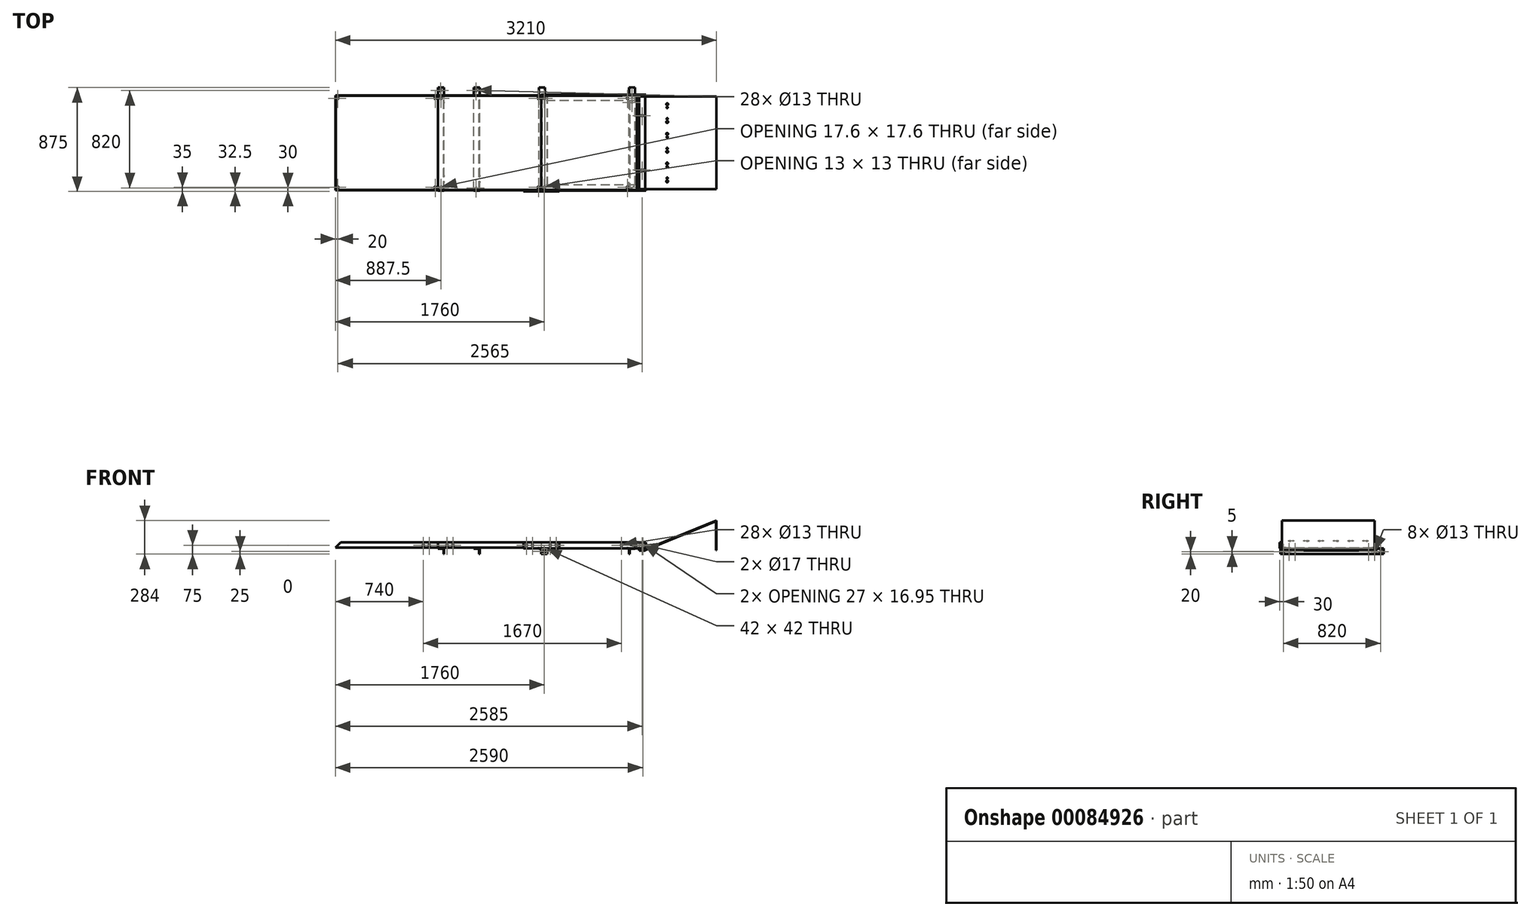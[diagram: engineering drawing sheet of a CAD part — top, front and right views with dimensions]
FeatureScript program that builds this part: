
annotation { "Feature Type Name" : "Feature", "Feature Type Description" : "" }
export const myFeature = defineFeature(function(context is Context, id is Id, definition is map)
    precondition{}
    {
        {
            var Q0;
            Q0=qCreatedBy(makeId("Front.planeOp"),FACE);
            var sketch = newSketch(context, id + "F0", { "sketchPlane" : qUnion([Q0])});
            skLineSegment(sketch, "E0", {"start": v(0, 0) * mm, "end": v(0, 4) * mm});
            skLineSegment(sketch, "E1", {"start": v(0, 4) * mm, "end": v(50, 4) * mm});
            skLineSegment(sketch, "E2", {"start": v(50, 4) * mm, "end": v(650, 250) * mm});
            skLineSegment(sketch, "E3", {"start": v(650, 250) * mm, "end": v(650, 0) * mm});
            skLineSegment(sketch, "E4", {"start": v(650, 0) * mm, "end": v(646, 0) * mm});
            skLineSegment(sketch, "E5", {"start": v(646, 0) * mm, "end": v(646, 244.04) * mm});
            skLineSegment(sketch, "E6", {"start": v(646, 244.04) * mm, "end": v(50.79, 0) * mm});
            skLineSegment(sketch, "E7", {"start": v(50.79, 0) * mm, "end": v(0, 0) * mm});
            skSolve(sketch);
        }
        {
            var Q0;
            Q0 = qSketchRegion(id + "F0", true);
            extrude(context, id + "F1", {"entities" : qUnion([Q0]), "oppositeDirection" : true, "depth" : 780 * mm});
        }
        {
            var Q0;
            Q0=qCreatedBy(makeId("Right.planeOp"),FACE);
            var sketch = newSketch(context, id + "F2", { "sketchPlane" : qUnion([Q0])});
            skLineSegment(sketch, "E8", {"start": v(0, 0) * mm, "end": v(-7, 0) * mm});
            skLineSegment(sketch, "E9", {"start": v(-7, 0) * mm, "end": v(-7, 66) * mm});
            skLineSegment(sketch, "E10", {"start": v(-7, 66) * mm, "end": v(-11, 66) * mm});
            skLineSegment(sketch, "E11", {"start": v(-11, 66) * mm, "end": v(-11, -4) * mm});
            skLineSegment(sketch, "E12", {"start": v(-11, -4) * mm, "end": v(791, -4) * mm});
            skLineSegment(sketch, "E13", {"start": v(791, -4) * mm, "end": v(791, 66) * mm});
            skLineSegment(sketch, "E14", {"start": v(791, 66) * mm, "end": v(787, 66) * mm});
            skLineSegment(sketch, "E15", {"start": v(787, 66) * mm, "end": v(787, 0) * mm});
            skLineSegment(sketch, "E16", {"start": v(787, 0) * mm, "end": v(0, 0) * mm});
            skSolve(sketch);
        }
        {
            var Q0;
            Q0=makeQuery(id+"F2.imprint","IMPRINT",FACE,{"disambiguationData":[TD([[makeQuery(id+"F2.imprint","IMPRINT",EDGE,{"derivedFrom":sQuery(id+"F2.wireOp",EDGE,"E8")}),1.0]])]});
            extrude(context, id + "F3", {"entities" : qUnion([Q0]), "depth" : 50 * mm});
        }
        {
            var Q0;
            Q0=makeQuery(id+"F3.opExtrude","SWEPT_FACE",FACE,{"disambiguationData":[OSD([sQuery(id+"F2.wireOp",EDGE,"E11")])]});
            var sketch = newSketch(context, id + "F4", { "sketchPlane" : qUnion([Q0])});
            skCircle(sketch, "E17", {"center": v(20, 41) * mm, "radius": 8.5 * mm});
            skSolve(sketch);
        }
        {
            var Q0;
            Q0 = qSketchRegion(id + "F4", true);
            extrude(context, id + "F5", {"entities" : qUnion([Q0]), "operationType" : NewBodyOperationType.REMOVE, "endBound" : BoundingType.THROUGH_ALL, "oppositeDirection" : true, "depth" : 25 * mm});
        }
        {
            var Q0;
            Q0=makeQuery(id+"F3.opExtrude","SWEPT_FACE",FACE,{"disambiguationData":[OSD([sQuery(id+"F2.wireOp",EDGE,"E11")])]});
            var sketch = newSketch(context, id + "F6", { "sketchPlane" : qUnion([Q0])});
            skLineSegment(sketch, "E18.bottom", {"start": v(55, 66) * mm, "end": v(-825, 66) * mm});
            skLineSegment(sketch, "E18.top", {"start": v(55, 16) * mm, "end": v(-825, 16) * mm});
            skLineSegment(sketch, "E18.left", {"start": v(55, 66) * mm, "end": v(55, 16) * mm});
            skLineSegment(sketch, "E18.right", {"start": v(-825, 66) * mm, "end": v(-825, 16) * mm});
            skSolve(sketch);
        }
        {
            var Q0;
            Q0 = qSketchRegion(id + "F6", true);
            extrude(context, id + "F7", {"entities" : qUnion([Q0]), "depth" : 4 * mm});
        }
        {
            var Q0;
            Q0=makeQuery(id+"F7.opExtrude","CAP_FACE",FACE,{"disambiguationData":[OSD([sQuery(id+"F6.wireOp",EDGE,"E18.bottom"),sQuery(id+"F6.wireOp",EDGE,"E18.top"),sQuery(id+"F6.wireOp",EDGE,"E18.left"),sQuery(id+"F6.wireOp",EDGE,"E18.right")])],"isStart":true});
            var sketch = newSketch(context, id + "F8", { "sketchPlane" : qUnion([Q0])});
            skLineSegment(sketch, "E19.bottom", {"start": v(20, 16) * mm, "end": v(825, 16) * mm});
            skLineSegment(sketch, "E19.top", {"start": v(20, 20) * mm, "end": v(825, 20) * mm});
            skLineSegment(sketch, "E19.left", {"start": v(20, 16) * mm, "end": v(20, 20) * mm});
            skLineSegment(sketch, "E19.right", {"start": v(825, 16) * mm, "end": v(825, 20) * mm});
            skSolve(sketch);
        }
        {
            var Q0;
            Q0 = qSketchRegion(id + "F8", true);
            extrude(context, id + "F9", {"entities" : qUnion([Q0]), "operationType" : NewBodyOperationType.ADD, "depth" : 46 * mm});
        }
        {
            var Q0;
            Q0=makeQuery(id+"F3.opExtrude","SWEPT_FACE",FACE,{"disambiguationData":[OSD([sQuery(id+"F2.wireOp",EDGE,"E13")])]});
            var sketch = newSketch(context, id + "F10", { "sketchPlane" : qUnion([Q0])});
            skLineSegment(sketch, "E20.bottom", {"start": v(-55, 66) * mm, "end": v(825, 66) * mm});
            skLineSegment(sketch, "E20.top", {"start": v(-55, 16) * mm, "end": v(825, 16) * mm});
            skLineSegment(sketch, "E20.left", {"start": v(-55, 66) * mm, "end": v(-55, 16) * mm});
            skLineSegment(sketch, "E20.right", {"start": v(825, 66) * mm, "end": v(825, 16) * mm});
            skSolve(sketch);
        }
        {
            var Q0;
            Q0 = qSketchRegion(id + "F10", true);
            extrude(context, id + "F11", {"entities" : qUnion([Q0]), "depth" : 4 * mm});
        }
        {
            var Q0;
            Q0=makeQuery(id+"F11.opExtrude","CAP_FACE",FACE,{"disambiguationData":[OSD([sQuery(id+"F10.wireOp",EDGE,"E20.bottom"),sQuery(id+"F10.wireOp",EDGE,"E20.top"),sQuery(id+"F10.wireOp",EDGE,"E20.left"),sQuery(id+"F10.wireOp",EDGE,"E20.right")])],"isStart":true});
            var sketch = newSketch(context, id + "F12", { "sketchPlane" : qUnion([Q0])});
            skLineSegment(sketch, "E21.bottom", {"start": v(-825, 16) * mm, "end": v(-20, 16) * mm});
            skLineSegment(sketch, "E21.top", {"start": v(-825, 20) * mm, "end": v(-20, 20) * mm});
            skLineSegment(sketch, "E21.left", {"start": v(-825, 16) * mm, "end": v(-825, 20) * mm});
            skLineSegment(sketch, "E21.right", {"start": v(-20, 16) * mm, "end": v(-20, 20) * mm});
            skSolve(sketch);
        }
        {
            var Q0;
            Q0=makeQuery(id+"F12.imprint","IMPRINT",FACE,{"disambiguationData":[TD([[makeQuery(id+"F12.imprint","IMPRINT",EDGE,{"derivedFrom":sQuery(id+"F12.wireOp",EDGE,"E21.bottom")}),-1.0]])]});
            extrude(context, id + "F13", {"entities" : qUnion([Q0]), "operationType" : NewBodyOperationType.ADD, "depth" : 46 * mm});
        }
        {
            var Q0;
            Q0=makeQuery(id+"F9.boolean.opBoolean","MERGE",FACE,{"derivedFrom":[makeQuery(id+"F7.opExtrude","SWEPT_FACE",FACE,{"disambiguationData":[OSD([sQuery(id+"F6.wireOp",EDGE,"E18.top")])]}),makeQuery(id+"F9.opExtrude","SWEPT_FACE",FACE,{"disambiguationData":[OSD([sQuery(id+"F8.wireOp",EDGE,"E19.bottom")])]})]});
            var sketch = newSketch(context, id + "F14", { "sketchPlane" : qUnion([Q0])});
            skLineSegment(sketch, "E22.bottom", {"start": v(-845, 15) * mm, "end": v(-795, 15) * mm});
            skLineSegment(sketch, "E22.top", {"start": v(-845, -855) * mm, "end": v(-795, -855) * mm});
            skLineSegment(sketch, "E22.left", {"start": v(-845, 15) * mm, "end": v(-845, -855) * mm});
            skLineSegment(sketch, "E22.right", {"start": v(-795, 15) * mm, "end": v(-795, -855) * mm});
            skLineSegment(sketch, "E23.bottom", {"start": v(-1645, 15) * mm, "end": v(-1695, 15) * mm});
            skLineSegment(sketch, "E23.top", {"start": v(-1645, -855) * mm, "end": v(-1695, -855) * mm});
            skLineSegment(sketch, "E23.left", {"start": v(-1645, 15) * mm, "end": v(-1645, -855) * mm});
            skLineSegment(sketch, "E23.right", {"start": v(-1695, 15) * mm, "end": v(-1695, -855) * mm});
            skLineSegment(sketch, "E24.bottom", {"start": v(-35.12, 15) * mm, "end": v(-85.12, 15) * mm});
            skLineSegment(sketch, "E24.top", {"start": v(-35.12, -855) * mm, "end": v(-85.12, -855) * mm});
            skLineSegment(sketch, "E24.left", {"start": v(-35.12, 15) * mm, "end": v(-35.12, -855) * mm});
            skLineSegment(sketch, "E24.right", {"start": v(-85.12, 15) * mm, "end": v(-85.12, -855) * mm});
            skSolve(sketch);
        }
        {
            var Q0;
            Q0 = qSketchRegion(id + "F14", true);
            extrude(context, id + "F15", {"entities" : qUnion([Q0]), "depth" : 4 * mm});
        }
        {
            var Q0;
            Q0=makeQuery(id+"F15.opExtrude","CAP_FACE",FACE,{"disambiguationData":[OSD([sQuery(id+"F14.wireOp",EDGE,"E23.bottom"),sQuery(id+"F14.wireOp",EDGE,"E23.top"),sQuery(id+"F14.wireOp",EDGE,"E23.left"),sQuery(id+"F14.wireOp",EDGE,"E23.right")])],"isStart":false});
            var sketch = newSketch(context, id + "F16", { "sketchPlane" : qUnion([Q0])});
            skLineSegment(sketch, "E25.bottom", {"start": v(-1645, 15) * mm, "end": v(-1649, 15) * mm});
            skLineSegment(sketch, "E25.top", {"start": v(-1645, -855) * mm, "end": v(-1649, -855) * mm});
            skLineSegment(sketch, "E25.left", {"start": v(-1645, 15) * mm, "end": v(-1645, -855) * mm});
            skLineSegment(sketch, "E25.right", {"start": v(-1649, 15) * mm, "end": v(-1649, -855) * mm});
            skSolve(sketch);
        }
        {
            var Q0;
            Q0 = qSketchRegion(id + "F16", true);
            extrude(context, id + "F17", {"entities" : qUnion([Q0]), "operationType" : NewBodyOperationType.ADD, "depth" : 46 * mm});
        }
        {
            var Q0;
            Q0=makeQuery(id+"F15.opExtrude","CAP_FACE",FACE,{"disambiguationData":[OSD([sQuery(id+"F14.wireOp",EDGE,"E22.bottom"),sQuery(id+"F14.wireOp",EDGE,"E22.top"),sQuery(id+"F14.wireOp",EDGE,"E22.left"),sQuery(id+"F14.wireOp",EDGE,"E22.right")])],"isStart":false});
            var sketch = newSketch(context, id + "F18", { "sketchPlane" : qUnion([Q0])});
            skLineSegment(sketch, "E26.bottom", {"start": v(-795, -855) * mm, "end": v(-799, -855) * mm});
            skLineSegment(sketch, "E26.top", {"start": v(-795, 15) * mm, "end": v(-799, 15) * mm});
            skLineSegment(sketch, "E26.left", {"start": v(-795, -855) * mm, "end": v(-795, 15) * mm});
            skLineSegment(sketch, "E26.right", {"start": v(-799, -855) * mm, "end": v(-799, 15) * mm});
            skSolve(sketch);
        }
        {
            var Q0;
            Q0 = qSketchRegion(id + "F18", true);
            extrude(context, id + "F19", {"entities" : qUnion([Q0]), "operationType" : NewBodyOperationType.ADD, "depth" : 44 * mm});
        }
        {
            var Q0;
            Q0=makeQuery(id+"F15.opExtrude","CAP_FACE",FACE,{"disambiguationData":[OSD([sQuery(id+"F14.wireOp",EDGE,"E24.bottom"),sQuery(id+"F14.wireOp",EDGE,"E24.top"),sQuery(id+"F14.wireOp",EDGE,"E24.left"),sQuery(id+"F14.wireOp",EDGE,"E24.right")])],"isStart":false});
            var sketch = newSketch(context, id + "F20", { "sketchPlane" : qUnion([Q0])});
            skLineSegment(sketch, "E27.bottom", {"start": v(-85.12, -855) * mm, "end": v(-81.12, -855) * mm});
            skLineSegment(sketch, "E27.top", {"start": v(-85.12, 15) * mm, "end": v(-81.12, 15) * mm});
            skLineSegment(sketch, "E27.left", {"start": v(-85.12, -855) * mm, "end": v(-85.12, 15) * mm});
            skLineSegment(sketch, "E27.right", {"start": v(-81.12, -855) * mm, "end": v(-81.12, 15) * mm});
            skSolve(sketch);
        }
        {
            var Q0;
            Q0 = qSketchRegion(id + "F20", true);
            extrude(context, id + "F21", {"entities" : qUnion([Q0]), "operationType" : NewBodyOperationType.ADD, "depth" : 46 * mm});
        }
        {
            var Q0;
            Q0=makeQuery(id+"F7.opExtrude","CAP_FACE",FACE,{"disambiguationData":[OSD([sQuery(id+"F6.wireOp",EDGE,"E18.bottom"),sQuery(id+"F6.wireOp",EDGE,"E18.top"),sQuery(id+"F6.wireOp",EDGE,"E18.left"),sQuery(id+"F6.wireOp",EDGE,"E18.right")])],"isStart":false});
            var sketch = newSketch(context, id + "F22", { "sketchPlane" : qUnion([Q0])});
            skCircle(sketch, "E28", {"center": v(30, 41) * mm, "radius": 8.5 * mm});
            skPoint(sketch, "E28.centerSnap0", {"position": v(55, 41) * mm});
            skSolve(sketch);
        }
        {
            var Q0;
            Q0 = qSketchRegion(id + "F22", true);
            extrude(context, id + "F23", {"entities" : qUnion([Q0]), "operationType" : NewBodyOperationType.REMOVE, "endBound" : BoundingType.THROUGH_ALL, "oppositeDirection" : true, "depth" : 25 * mm});
        }
        {
            var Q0;
            Q0=makeQuery(id+"F11.opExtrude","CAP_FACE",FACE,{"disambiguationData":[OSD([sQuery(id+"F10.wireOp",EDGE,"E20.bottom"),sQuery(id+"F10.wireOp",EDGE,"E20.top"),sQuery(id+"F10.wireOp",EDGE,"E20.left"),sQuery(id+"F10.wireOp",EDGE,"E20.right")])],"isStart":false});
            var sketch = newSketch(context, id + "F24", { "sketchPlane" : qUnion([Q0])});
            skSolve(sketch);
        }
        {
            var Q0;
            Q0=makeQuery(id+"F11.opExtrude","CAP_FACE",FACE,{"disambiguationData":[OSD([sQuery(id+"F10.wireOp",EDGE,"E20.bottom"),sQuery(id+"F10.wireOp",EDGE,"E20.top"),sQuery(id+"F10.wireOp",EDGE,"E20.left"),sQuery(id+"F10.wireOp",EDGE,"E20.right")])],"isStart":true});
            var sketch = newSketch(context, id + "F25", { "sketchPlane" : qUnion([Q0])});
            skCircle(sketch, "E29", {"center": v(30, 41) * mm, "radius": 8.5 * mm});
            skPoint(sketch, "E29.centerSnap0", {"position": v(55, 41) * mm});
            skSolve(sketch);
        }
        {
            var Q0;
            Q0 = qSketchRegion(id + "F25", true);
            extrude(context, id + "F26", {"entities" : qUnion([Q0]), "operationType" : NewBodyOperationType.REMOVE, "endBound" : BoundingType.THROUGH_ALL, "oppositeDirection" : true, "depth" : 25 * mm});
        }
        {
            var Q0;
            Q0=makeQuery(id+"F1.opExtrude","SWEPT_FACE",FACE,{"disambiguationData":[OSD([sQuery(id+"F0.wireOp",EDGE,"E2")])]});
            var sketch = newSketch(context, id + "F27", { "sketchPlane" : qUnion([Q0])});
            skCircle(sketch, "E30", {"center": v(247.78, 715) * mm, "radius": 8.5 * mm});
            skCircle(sketch, "E31", {"center": v(247.78, 565) * mm, "radius": 8.5 * mm});
            skCircle(sketch, "E32", {"center": v(247.78, 465) * mm, "radius": 8.5 * mm});
            skCircle(sketch, "E33", {"center": v(247.78, 315) * mm, "radius": 8.5 * mm});
            skCircle(sketch, "E34", {"center": v(247.78, 215) * mm, "radius": 8.5 * mm});
            skCircle(sketch, "E35", {"center": v(247.78, 65) * mm, "radius": 8.5 * mm});
            skCircle(sketch, "E36", {"center": v(247.78, 688) * mm, "radius": 5.75 * mm});
            skCircle(sketch, "E37", {"center": v(247.78, 592) * mm, "radius": 5.75 * mm});
            skCircle(sketch, "E38", {"center": v(247.78, 438) * mm, "radius": 5.75 * mm});
            skCircle(sketch, "E39", {"center": v(247.78, 342) * mm, "radius": 5.75 * mm});
            skCircle(sketch, "E40", {"center": v(247.78, 188) * mm, "radius": 5.75 * mm});
            skCircle(sketch, "E41", {"center": v(247.78, 92) * mm, "radius": 5.75 * mm});
            skSolve(sketch);
        }
        {
            var Q0;
            Q0 = qSketchRegion(id + "F27", true);
            extrude(context, id + "F28", {"entities" : qUnion([Q0]), "operationType" : NewBodyOperationType.REMOVE, "endBound" : BoundingType.THROUGH_ALL, "oppositeDirection" : true, "depth" : 25 * mm});
        }
        {
            var Q0;
            Q0=makeQuery(id+"F3.opExtrude","SWEPT_FACE",FACE,{"disambiguationData":[OSD([sQuery(id+"F2.wireOp",EDGE,"E12")])]});
            var sketch = newSketch(context, id + "F29", { "sketchPlane" : qUnion([Q0])});
            skCircle(sketch, "E42", {"center": v(25, -619) * mm, "radius": 6 * mm});
            skPoint(sketch, "E42.centerSnap0", {"position": v(25, -791) * mm});
            skCircle(sketch, "E43", {"center": v(25, -161) * mm, "radius": 6 * mm});
            skPoint(sketch, "E43.centerSnap0", {"position": v(25, 11) * mm});
            skLineSegment(sketch, "E44", {"start": v(50, -390) * mm, "end": v(0, -390) * mm});
            skSolve(sketch);
        }
        {
            var Q0;
            Q0 = qSketchRegion(id + "F29", true);
            extrude(context, id + "F30", {"entities" : qUnion([Q0]), "operationType" : NewBodyOperationType.REMOVE, "endBound" : BoundingType.THROUGH_ALL, "oppositeDirection" : true, "depth" : 25 * mm});
        }
        {
            var Q0;
            Q0=makeQuery(id+"F1.opExtrude","SWEPT_FACE",FACE,{"disambiguationData":[OSD([sQuery(id+"F0.wireOp",EDGE,"E1")])]});
            var sketch = newSketch(context, id + "F31", { "sketchPlane" : qUnion([Q0])});
            skCircle(sketch, "E45", {"center": v(25, 619) * mm, "radius": 6.5 * mm});
            skPoint(sketch, "E45.centerSnap0", {"position": v(25, 780) * mm});
            skCircle(sketch, "E46", {"center": v(25, 161) * mm, "radius": 6.5 * mm});
            skLineSegment(sketch, "E47", {"start": v(50, 390) * mm, "end": v(0, 390) * mm});
            skSolve(sketch);
        }
        {
            var Q0;
            Q0 = qSketchRegion(id + "F31", true);
            extrude(context, id + "F32", {"entities" : qUnion([Q0]), "operationType" : NewBodyOperationType.REMOVE, "endBound" : BoundingType.THROUGH_ALL, "oppositeDirection" : true, "depth" : 25 * mm});
        }
        {
            var Q0;
            Q0=makeQuery(id+"F7.opExtrude","CAP_FACE",FACE,{"disambiguationData":[OSD([sQuery(id+"F6.wireOp",EDGE,"E18.bottom"),sQuery(id+"F6.wireOp",EDGE,"E18.top"),sQuery(id+"F6.wireOp",EDGE,"E18.left"),sQuery(id+"F6.wireOp",EDGE,"E18.right")])],"isStart":false});
            var sketch = newSketch(context, id + "F33", { "sketchPlane" : qUnion([Q0])});
            skLineSegment(sketch, "E48.bottom", {"start": v(-825, 16) * mm, "end": v(-775, 16) * mm});
            skLineSegment(sketch, "E48.top", {"start": v(-825, -34) * mm, "end": v(-775, -34) * mm});
            skLineSegment(sketch, "E48.left", {"start": v(-825, 16) * mm, "end": v(-825, -34) * mm});
            skLineSegment(sketch, "E48.right", {"start": v(-775, 16) * mm, "end": v(-775, -34) * mm});
            skLineSegment(sketch, "E49.0", {"start": v(-779, 12) * mm, "end": v(-779, -30) * mm});
            skLineSegment(sketch, "E49.1", {"start": v(-821, 12) * mm, "end": v(-779, 12) * mm});
            skLineSegment(sketch, "E49.2", {"start": v(-821, 12) * mm, "end": v(-821, -30) * mm});
            skLineSegment(sketch, "E49.3", {"start": v(-821, -30) * mm, "end": v(-779, -30) * mm});
            skSolve(sketch);
        }
        {
            var Q0;
            Q0=makeQuery(id+"F33.imprint","IMPRINT",FACE,{"disambiguationData":[TD([[makeQuery(id+"F33.imprint","IMPRINT",EDGE,{"derivedFrom":sQuery(id+"F33.wireOp",EDGE,"E48.bottom")}),1.0]])]});
            extrude(context, id + "F34", {"entities" : qUnion([Q0]), "oppositeDirection" : true, "depth" : 810 * mm});
        }
        {
            var Q0;
            Q0=makeQuery(id+"F15.opExtrude","SWEPT_BODY",BODY,{"disambiguationData":[OSD([sQuery(id+"F14.wireOp",EDGE,"E23.bottom"),sQuery(id+"F14.wireOp",EDGE,"E23.top"),sQuery(id+"F14.wireOp",EDGE,"E23.left"),sQuery(id+"F14.wireOp",EDGE,"E23.right")])]});
            transform(context, id + "F35", {"entities" : qUnion([Q0]), "transformType" : TransformType.TRANSLATION_3D, "dx" : 300 * mm, "dy" : 0 * mm, "dz" : 0 * mm, "makeCopy" : true});
        }
        {
            var Q0;
            Q0=makeQuery(id+"F7.opExtrude","CAP_FACE",FACE,{"disambiguationData":[OSD([sQuery(id+"F6.wireOp",EDGE,"E18.bottom"),sQuery(id+"F6.wireOp",EDGE,"E18.top"),sQuery(id+"F6.wireOp",EDGE,"E18.left"),sQuery(id+"F6.wireOp",EDGE,"E18.right")])],"isStart":false});
            var sketch = newSketch(context, id + "F36", { "sketchPlane" : qUnion([Q0])});
            skLineSegment(sketch, "E50.bottom", {"start": v(-675, 16) * mm, "end": v(-975, 16) * mm});
            skLineSegment(sketch, "E50.top", {"start": v(-675, 66) * mm, "end": v(-975, 66) * mm});
            skLineSegment(sketch, "E50.left", {"start": v(-675, 16) * mm, "end": v(-675, 66) * mm});
            skLineSegment(sketch, "E50.right", {"start": v(-975, 16) * mm, "end": v(-975, 66) * mm});
            skCircle(sketch, "E51", {"center": v(-700, 41) * mm, "radius": 6.5 * mm});
            skPoint(sketch, "E51.centerSnap0", {"position": v(-675, 41) * mm});
            skCircle(sketch, "E52", {"center": v(-750, 41) * mm, "radius": 6.5 * mm});
            skCircle(sketch, "E53", {"center": v(-900, 41) * mm, "radius": 6.5 * mm});
            skCircle(sketch, "E54", {"center": v(-950, 41) * mm, "radius": 6.5 * mm});
            skSolve(sketch);
        }
        {
            var Q0;
            Q0 = qSketchRegion(id + "F36", true);
            var Q1;
            {var subQ2=sQuery(id+"F36.wireOp",EDGE,"E50.right");Q1=makeQuery(id+"F36.imprint","IMPRINT",FACE,{"disambiguationData":[TD([[makeQuery(id+"F36.imprint","IMPRINT",EDGE,{"derivedFrom":subQ2}),-1.0]])]});}
            extrude(context, id + "F37", {"entities" : qUnion([Q0, Q1]), "depth" : 5 * mm});
        }
        {
            var Q0;
            Q0=makeQuery(id+"F7.opExtrude","CAP_FACE",FACE,{"disambiguationData":[OSD([sQuery(id+"F6.wireOp",EDGE,"E18.bottom"),sQuery(id+"F6.wireOp",EDGE,"E18.top"),sQuery(id+"F6.wireOp",EDGE,"E18.left"),sQuery(id+"F6.wireOp",EDGE,"E18.right")])],"isStart":false});
            var sketch = newSketch(context, id + "F38", { "sketchPlane" : qUnion([Q0])});
            skCircle(sketch, "E55", {"center": v(-750, 41) * mm, "radius": 6.5 * mm});
            skPoint(sketch, "E55.centerSnap0", {"position": v(-825, 41) * mm});
            skCircle(sketch, "E56", {"center": v(-700, 41) * mm, "radius": 6.5 * mm});
            skSolve(sketch);
        }
        {
            var Q0;
            Q0=makeQuery(id+"F38.imprint","IMPRINT",FACE,{"disambiguationData":[TD([[makeQuery(id+"F38.imprint","IMPRINT",EDGE,{"derivedFrom":sQuery(id+"F38.wireOp",EDGE,"E55")}),1.0]])]});
            var Q1;
            Q1=makeQuery(id+"F38.imprint","IMPRINT",FACE,{"disambiguationData":[TD([[makeQuery(id+"F38.imprint","IMPRINT",EDGE,{"derivedFrom":sQuery(id+"F38.wireOp",EDGE,"E56")}),1.0]])]});
            extrude(context, id + "F39", {"entities" : qUnion([Q0, Q1]), "operationType" : NewBodyOperationType.REMOVE, "endBound" : BoundingType.THROUGH_ALL, "oppositeDirection" : true, "depth" : 25 * mm});
        }
        {
            var Q0;
            Q0=makeQuery(id+"F24.imprint","IMPRINT",FACE,{"disambiguationData":[TD([[makeQuery(id+"F24.imprint","IMPRINT",EDGE,{"derivedFrom":makeQuery(id+"F11.opExtrude","CAP_EDGE",EDGE,{"disambiguationData":[OSD([sQuery(id+"F10.wireOp",EDGE,"E20.bottom")])],"isStart":false})}),-1.0]])]});
            var sketch = newSketch(context, id + "F40", { "sketchPlane" : qUnion([Q0])});
            skCircle(sketch, "E57", {"center": v(750, 41) * mm, "radius": 6.5 * mm});
            skCircle(sketch, "E58", {"center": v(700, 41) * mm, "radius": 6.5 * mm});
            skSolve(sketch);
        }
        {
            var Q0;
            Q0=makeQuery(id+"F40.imprint","IMPRINT",FACE,{"disambiguationData":[TD([[makeQuery(id+"F40.imprint","IMPRINT",EDGE,{"derivedFrom":sQuery(id+"F40.wireOp",EDGE,"E58")}),1.0]])]});
            var Q1;
            Q1=makeQuery(id+"F40.imprint","IMPRINT",FACE,{"disambiguationData":[TD([[makeQuery(id+"F40.imprint","IMPRINT",EDGE,{"derivedFrom":sQuery(id+"F40.wireOp",EDGE,"E57")}),1.0]])]});
            extrude(context, id + "F41", {"entities" : qUnion([Q0, Q1]), "operationType" : NewBodyOperationType.REMOVE, "endBound" : BoundingType.THROUGH_ALL, "oppositeDirection" : true, "depth" : 25 * mm});
        }
        {
            var Q0;
            Q0=makeQuery(id+"F17.boolean.opBoolean","MERGE",FACE,{"derivedFrom":[makeQuery(id+"F15.opExtrude","SWEPT_FACE",FACE,{"disambiguationData":[OSD([sQuery(id+"F14.wireOp",EDGE,"E23.left")])]}),makeQuery(id+"F17.opExtrude","SWEPT_FACE",FACE,{"disambiguationData":[OSD([sQuery(id+"F16.wireOp",EDGE,"E25.left")])]})]});
            var sketch = newSketch(context, id + "F42", { "sketchPlane" : qUnion([Q0])});
            skCircle(sketch, "E59", {"center": v(60, -9) * mm, "radius": 6.5 * mm});
            skPoint(sketch, "E59.centerSnap0", {"position": v(-15, -9) * mm});
            skPoint(sketch, "E59.perimeterSnap0", {"position": v(-15, -9) * mm});
            skCircle(sketch, "E60", {"center": v(110, -9) * mm, "radius": 6.5 * mm});
            skCircle(sketch, "E61", {"center": v(780, -9) * mm, "radius": 6.5 * mm});
            skPoint(sketch, "E61.centerSnap0", {"position": v(855, -9) * mm});
            skCircle(sketch, "E62", {"center": v(730, -9) * mm, "radius": 6.5 * mm});
            skSolve(sketch);
        }
        {
            var Q0;
            Q0 = qSketchRegion(id + "F42", true);
            extrude(context, id + "F43", {"entities" : qUnion([Q0]), "operationType" : NewBodyOperationType.REMOVE, "oppositeDirection" : true, "depth" : 25 * mm});
        }
        {
            var Q0;
            Q0=makeQuery(id+"F35.opPattern","COPY",FACE,{"derivedFrom":makeQuery(id+"F17.boolean.opBoolean","MERGE",FACE,{"derivedFrom":[makeQuery(id+"F15.opExtrude","SWEPT_FACE",FACE,{"disambiguationData":[OSD([sQuery(id+"F14.wireOp",EDGE,"E23.left")])]}),makeQuery(id+"F17.opExtrude","SWEPT_FACE",FACE,{"disambiguationData":[OSD([sQuery(id+"F16.wireOp",EDGE,"E25.left")])]})]}),"instanceName":"1"});
            var sketch = newSketch(context, id + "F44", { "sketchPlane" : qUnion([Q0])});
            skCircle(sketch, "E63", {"center": v(60, -9) * mm, "radius": 6.5 * mm});
            skPoint(sketch, "E63.centerSnap0", {"position": v(-15, -9) * mm});
            skCircle(sketch, "E64", {"center": v(110, -9) * mm, "radius": 6.5 * mm});
            skSolve(sketch);
        }
        {
            var Q0;
            Q0=makeQuery(id+"F44.imprint","IMPRINT",FACE,{"disambiguationData":[TD([[makeQuery(id+"F44.imprint","IMPRINT",EDGE,{"derivedFrom":sQuery(id+"F44.wireOp",EDGE,"E63")}),1.0]])]});
            var Q1;
            Q1=makeQuery(id+"F44.imprint","IMPRINT",FACE,{"disambiguationData":[TD([[makeQuery(id+"F44.imprint","IMPRINT",EDGE,{"derivedFrom":sQuery(id+"F44.wireOp",EDGE,"E64")}),1.0]])]});
            extrude(context, id + "F45", {"entities" : qUnion([Q0, Q1]), "operationType" : NewBodyOperationType.REMOVE, "endBound" : BoundingType.THROUGH_ALL, "oppositeDirection" : true, "depth" : 25 * mm});
        }
        {
            var Q0;
            Q0=makeQuery(id+"F35.opPattern","COPY",BODY,{"derivedFrom":makeQuery(id+"F15.opExtrude","SWEPT_BODY",BODY,{"disambiguationData":[OSD([sQuery(id+"F14.wireOp",EDGE,"E23.bottom"),sQuery(id+"F14.wireOp",EDGE,"E23.top"),sQuery(id+"F14.wireOp",EDGE,"E23.left"),sQuery(id+"F14.wireOp",EDGE,"E23.right")])]}),"instanceName":"1"});
            transform(context, id + "F46", {"entities" : qUnion([Q0]), "transformType" : TransformType.TRANSLATION_3D, "dx" : 150 * mm, "dy" : 0 * mm, "dz" : 0 * mm, "makeCopy" : true});
        }
        {
            var Q0;
            Q0=makeQuery(id+"F35.opPattern","COPY",BODY,{"derivedFrom":makeQuery(id+"F15.opExtrude","SWEPT_BODY",BODY,{"disambiguationData":[OSD([sQuery(id+"F14.wireOp",EDGE,"E23.bottom"),sQuery(id+"F14.wireOp",EDGE,"E23.top"),sQuery(id+"F14.wireOp",EDGE,"E23.left"),sQuery(id+"F14.wireOp",EDGE,"E23.right")])]}),"instanceName":"1"});
            transform(context, id + "F47", {"entities" : qUnion([Q0]), "transformType" : TransformType.TRANSLATION_3D, "dx" : 250 * mm, "dy" : 0 * mm, "dz" : 0 * mm, "makeCopy" : true});
        }
        {
            var Q0;
            Q0=makeQuery(id+"F47.opPattern","COPY",BODY,{"derivedFrom":makeQuery(id+"F35.opPattern","COPY",BODY,{"derivedFrom":makeQuery(id+"F15.opExtrude","SWEPT_BODY",BODY,{"disambiguationData":[OSD([sQuery(id+"F14.wireOp",EDGE,"E23.bottom"),sQuery(id+"F14.wireOp",EDGE,"E23.top"),sQuery(id+"F14.wireOp",EDGE,"E23.left"),sQuery(id+"F14.wireOp",EDGE,"E23.right")])]}),"instanceName":"1"}),"instanceName":"1"});
            deleteBodies(context, id + "F48", {"entities" : qUnion([Q0])});
        }
        {
            var Q0;
            Q0=makeQuery(id+"F46.opPattern","COPY",BODY,{"derivedFrom":makeQuery(id+"F35.opPattern","COPY",BODY,{"derivedFrom":makeQuery(id+"F15.opExtrude","SWEPT_BODY",BODY,{"disambiguationData":[OSD([sQuery(id+"F14.wireOp",EDGE,"E23.bottom"),sQuery(id+"F14.wireOp",EDGE,"E23.top"),sQuery(id+"F14.wireOp",EDGE,"E23.left"),sQuery(id+"F14.wireOp",EDGE,"E23.right")])]}),"instanceName":"1"}),"instanceName":"1"});
            deleteBodies(context, id + "F49", {"entities" : qUnion([Q0])});
        }
        {
            var Q0;
            Q0=makeQuery(id+"F15.opExtrude","CAP_FACE",FACE,{"disambiguationData":[OSD([sQuery(id+"F14.wireOp",EDGE,"E24.bottom"),sQuery(id+"F14.wireOp",EDGE,"E24.top"),sQuery(id+"F14.wireOp",EDGE,"E24.left"),sQuery(id+"F14.wireOp",EDGE,"E24.right")])],"isStart":true});
            var sketch = newSketch(context, id + "F50", { "sketchPlane" : qUnion([Q0])});
            skCircle(sketch, "E65", {"center": v(-60.12, 780) * mm, "radius": 6.5 * mm});
            skCircle(sketch, "E66", {"center": v(-60.12, 730) * mm, "radius": 6.5 * mm});
            skSolve(sketch);
        }
        {
            var Q0;
            Q0 = qSketchRegion(id + "F50", true);
            extrude(context, id + "F51", {"entities" : qUnion([Q0]), "operationType" : NewBodyOperationType.REMOVE, "oppositeDirection" : true, "depth" : 25 * mm});
        }
        {
            var Q0;
            Q0=makeQuery(id+"F34.opExtrude","SWEPT_FACE",FACE,{"disambiguationData":[OSD([sQuery(id+"F33.wireOp",EDGE,"E48.bottom")])]});
            var sketch = newSketch(context, id + "F52", { "sketchPlane" : qUnion([Q0])});
            skCircle(sketch, "E67", {"center": v(-800, 15) * mm, "radius": 6.5 * mm});
            skPoint(sketch, "E67.centerSnap0", {"position": v(-800, -15) * mm});
            skCircle(sketch, "E68", {"center": v(-800, 765) * mm, "radius": 6.5 * mm});
            skSolve(sketch);
        }
        {
            var Q0;
            Q0=makeQuery(id+"F35.opPattern","COPY",FACE,{"derivedFrom":makeQuery(id+"F17.boolean.opBoolean","MERGE",FACE,{"derivedFrom":[makeQuery(id+"F15.opExtrude","SWEPT_FACE",FACE,{"disambiguationData":[OSD([sQuery(id+"F14.wireOp",EDGE,"E23.left")])]}),makeQuery(id+"F17.opExtrude","SWEPT_FACE",FACE,{"disambiguationData":[OSD([sQuery(id+"F16.wireOp",EDGE,"E25.left")])]})]}),"instanceName":"1"});
            var sketch = newSketch(context, id + "F53", { "sketchPlane" : qUnion([Q0])});
            skLineSegment(sketch, "E69", {"start": v(855, 16) * mm, "end": v(805, -34) * mm});
            skLineSegment(sketch, "E70", {"start": v(805, -34) * mm, "end": v(855, -34) * mm});
            skLineSegment(sketch, "E71", {"start": v(855, -34) * mm, "end": v(855, 16) * mm});
            skSolve(sketch);
        }
        {
            var Q0;
            Q0 = qSketchRegion(id + "F53", true);
            extrude(context, id + "F54", {"entities" : qUnion([Q0]), "operationType" : NewBodyOperationType.REMOVE, "endBound" : BoundingType.THROUGH_ALL, "oppositeDirection" : true, "depth" : 25 * mm});
        }
        {
            var Q0;
            Q0=makeQuery(id+"F15.opExtrude","CAP_FACE",FACE,{"disambiguationData":[OSD([sQuery(id+"F14.wireOp",EDGE,"E24.bottom"),sQuery(id+"F14.wireOp",EDGE,"E24.top"),sQuery(id+"F14.wireOp",EDGE,"E24.left"),sQuery(id+"F14.wireOp",EDGE,"E24.right")])],"isStart":true});
            var sketch = newSketch(context, id + "F55", { "sketchPlane" : qUnion([Q0])});
            skSolve(sketch);
        }
        {
            var Q0;
            Q0=makeQuery(id+"F55.imprint","IMPRINT",FACE,{"disambiguationData":[TD([[makeQuery(id+"F55.imprint","IMPRINT",EDGE,{"derivedFrom":makeQuery(id+"F15.opExtrude","CAP_EDGE",EDGE,{"disambiguationData":[OSD([sQuery(id+"F14.wireOp",EDGE,"E24.bottom")])],"isStart":true})}),-1.0]])]});
            var sketch = newSketch(context, id + "F56", { "sketchPlane" : qUnion([Q0])});
            skLineSegment(sketch, "E72", {"start": v(-35.12, 35) * mm, "end": v(-85.12, -15) * mm});
            skLineSegment(sketch, "E73", {"start": v(-85.12, -15) * mm, "end": v(-35.12, -15) * mm});
            skLineSegment(sketch, "E74", {"start": v(-35.12, -15) * mm, "end": v(-35.12, 35) * mm});
            skSolve(sketch);
        }
        {
            var Q0;
            Q0=makeQuery(id+"F56.imprint","IMPRINT",FACE,{"disambiguationData":[TD([[makeQuery(id+"F56.imprint","IMPRINT",EDGE,{"derivedFrom":sQuery(id+"F56.wireOp",EDGE,"E72")}),1.0]])]});
            extrude(context, id + "F57", {"entities" : qUnion([Q0]), "operationType" : NewBodyOperationType.REMOVE, "endBound" : BoundingType.THROUGH_ALL, "oppositeDirection" : true, "depth" : 25 * mm});
        }
        {
            var Q0;
            Q0=makeQuery(id+"F52.imprint","IMPRINT",FACE,{"disambiguationData":[TD([[makeQuery(id+"F52.imprint","IMPRINT",EDGE,{"derivedFrom":sQuery(id+"F52.wireOp",EDGE,"E68")}),1.0]])]});
            var Q1;
            Q1=makeQuery(id+"F52.imprint","IMPRINT",FACE,{"disambiguationData":[TD([[makeQuery(id+"F52.imprint","IMPRINT",EDGE,{"derivedFrom":sQuery(id+"F52.wireOp",EDGE,"E67")}),1.0]])]});
            extrude(context, id + "F58", {"entities" : qUnion([Q0, Q1]), "operationType" : NewBodyOperationType.REMOVE, "oppositeDirection" : true, "depth" : 25 * mm});
        }
        {
            var Q0;
            Q0=makeQuery(id+"F9.opExtrude","SWEPT_FACE",FACE,{"disambiguationData":[OSD([sQuery(id+"F8.wireOp",EDGE,"E19.top")])]});
            var sketch = newSketch(context, id + "F59", { "sketchPlane" : qUnion([Q0])});
            skCircle(sketch, "E75", {"center": v(-800, 15) * mm, "radius": 6.5 * mm});
            skCircle(sketch, "E76", {"center": v(-100, 15) * mm, "radius": 6.5 * mm});
            skSolve(sketch);
        }
        {
            var Q0;
            Q0=makeQuery(id+"F59.imprint","IMPRINT",FACE,{"disambiguationData":[TD([[makeQuery(id+"F59.imprint","IMPRINT",EDGE,{"derivedFrom":sQuery(id+"F59.wireOp",EDGE,"E76")}),1.0]])]});
            var Q1;
            Q1=makeQuery(id+"F59.imprint","IMPRINT",FACE,{"disambiguationData":[TD([[makeQuery(id+"F59.imprint","IMPRINT",EDGE,{"derivedFrom":sQuery(id+"F59.wireOp",EDGE,"E75")}),1.0]])]});
            extrude(context, id + "F60", {"entities" : qUnion([Q0, Q1]), "operationType" : NewBodyOperationType.REMOVE, "oppositeDirection" : true, "depth" : 25 * mm});
        }
        {
            var Q0;
            Q0=makeQuery(id+"F13.opExtrude","SWEPT_FACE",FACE,{"disambiguationData":[OSD([sQuery(id+"F12.wireOp",EDGE,"E21.top")])]});
            var sketch = newSketch(context, id + "F61", { "sketchPlane" : qUnion([Q0])});
            skCircle(sketch, "E77", {"center": v(-800, 765) * mm, "radius": 6.5 * mm});
            skCircle(sketch, "E78", {"center": v(-100, 765) * mm, "radius": 6.5 * mm});
            skSolve(sketch);
        }
        {
            var Q0;
            Q0=makeQuery(id+"F61.imprint","IMPRINT",FACE,{"disambiguationData":[TD([[makeQuery(id+"F61.imprint","IMPRINT",EDGE,{"derivedFrom":sQuery(id+"F61.wireOp",EDGE,"E78")}),1.0]])]});
            var Q1;
            Q1=makeQuery(id+"F61.imprint","IMPRINT",FACE,{"disambiguationData":[TD([[makeQuery(id+"F61.imprint","IMPRINT",EDGE,{"derivedFrom":sQuery(id+"F61.wireOp",EDGE,"E77")}),1.0]])]});
            extrude(context, id + "F62", {"entities" : qUnion([Q0, Q1]), "operationType" : NewBodyOperationType.REMOVE, "oppositeDirection" : true, "depth" : 25 * mm});
        }
        {
            var Q0;
            Q0=makeQuery(id+"F15.opExtrude","CAP_FACE",FACE,{"disambiguationData":[OSD([sQuery(id+"F14.wireOp",EDGE,"E23.bottom"),sQuery(id+"F14.wireOp",EDGE,"E23.top"),sQuery(id+"F14.wireOp",EDGE,"E23.left"),sQuery(id+"F14.wireOp",EDGE,"E23.right")])],"isStart":false});
            var sketch = newSketch(context, id + "F63", { "sketchPlane" : qUnion([Q0])});
            skCircle(sketch, "E79", {"center": v(-1675, -830) * mm, "radius": 6.5 * mm});
            skCircle(sketch, "E80", {"center": v(-1675, -10) * mm, "radius": 6.5 * mm});
            skSolve(sketch);
        }
        {
            var Q0;
            Q0=makeQuery(id+"F63.imprint","IMPRINT",FACE,{"disambiguationData":[TD([[makeQuery(id+"F63.imprint","IMPRINT",EDGE,{"derivedFrom":sQuery(id+"F63.wireOp",EDGE,"E79")}),1.0]])]});
            var Q1;
            Q1=makeQuery(id+"F63.imprint","IMPRINT",FACE,{"disambiguationData":[TD([[makeQuery(id+"F63.imprint","IMPRINT",EDGE,{"derivedFrom":sQuery(id+"F63.wireOp",EDGE,"E80")}),1.0]])]});
            extrude(context, id + "F64", {"entities" : qUnion([Q0, Q1]), "operationType" : NewBodyOperationType.REMOVE, "oppositeDirection" : true, "depth" : 25 * mm});
        }
        {
            var Q0;
            Q0=makeQuery(id+"F35.opPattern","COPY",FACE,{"derivedFrom":makeQuery(id+"F15.opExtrude","CAP_FACE",FACE,{"disambiguationData":[OSD([sQuery(id+"F14.wireOp",EDGE,"E23.bottom"),sQuery(id+"F14.wireOp",EDGE,"E23.top"),sQuery(id+"F14.wireOp",EDGE,"E23.left"),sQuery(id+"F14.wireOp",EDGE,"E23.right")])],"isStart":false}),"instanceName":"1"});
            var sketch = newSketch(context, id + "F65", { "sketchPlane" : qUnion([Q0])});
            skCircle(sketch, "E81", {"center": v(-1375, -830) * mm, "radius": 6.5 * mm});
            skCircle(sketch, "E82", {"center": v(-1375, -10) * mm, "radius": 6.5 * mm});
            skSolve(sketch);
        }
        {
            var Q0;
            Q0=makeQuery(id+"F65.imprint","IMPRINT",FACE,{"disambiguationData":[TD([[makeQuery(id+"F65.imprint","IMPRINT",EDGE,{"derivedFrom":sQuery(id+"F65.wireOp",EDGE,"E81")}),1.0]])]});
            var Q1;
            Q1=makeQuery(id+"F65.imprint","IMPRINT",FACE,{"disambiguationData":[TD([[makeQuery(id+"F65.imprint","IMPRINT",EDGE,{"derivedFrom":sQuery(id+"F65.wireOp",EDGE,"E82")}),1.0]])]});
            extrude(context, id + "F66", {"entities" : qUnion([Q0, Q1]), "operationType" : NewBodyOperationType.REMOVE, "oppositeDirection" : true, "depth" : 25 * mm});
        }
        {
            var Q0;
            Q0=makeQuery(id+"F21.opExtrude","SWEPT_FACE",FACE,{"disambiguationData":[OSD([sQuery(id+"F20.wireOp",EDGE,"E27.right")])]});
            var sketch = newSketch(context, id + "F67", { "sketchPlane" : qUnion([Q0])});
            skCircle(sketch, "E83", {"center": v(830, -14) * mm, "radius": 6.5 * mm});
            skCircle(sketch, "E84", {"center": v(10, -14) * mm, "radius": 6.5 * mm});
            skSolve(sketch);
        }
        {
            var Q0;
            Q0=makeQuery(id+"F67.imprint","IMPRINT",FACE,{"disambiguationData":[TD([[makeQuery(id+"F67.imprint","IMPRINT",EDGE,{"derivedFrom":sQuery(id+"F67.wireOp",EDGE,"E83")}),1.0]])]});
            var Q1;
            Q1=makeQuery(id+"F67.imprint","IMPRINT",FACE,{"disambiguationData":[TD([[makeQuery(id+"F67.imprint","IMPRINT",EDGE,{"derivedFrom":sQuery(id+"F67.wireOp",EDGE,"E84")}),1.0]])]});
            extrude(context, id + "F68", {"entities" : qUnion([Q0, Q1]), "operationType" : NewBodyOperationType.REMOVE, "oppositeDirection" : true, "depth" : 25 * mm});
        }
        {
            var Q0;
            Q0=makeQuery(id+"F9.opExtrude","SWEPT_FACE",FACE,{"disambiguationData":[OSD([sQuery(id+"F8.wireOp",EDGE,"E19.top")])]});
            var sketch = newSketch(context, id + "F69", { "sketchPlane" : qUnion([Q0])});
            skLineSegment(sketch, "E85.bottom", {"start": v(-825, -11) * mm, "end": v(-20, -11) * mm});
            skLineSegment(sketch, "E85.top", {"start": v(-825, 788.5) * mm, "end": v(-20, 788.5) * mm});
            skLineSegment(sketch, "E85.left", {"start": v(-825, -11) * mm, "end": v(-825, 788.5) * mm});
            skLineSegment(sketch, "E85.right", {"start": v(-20, -11) * mm, "end": v(-20, 788.5) * mm});
            skLineSegment(sketch, "E86", {"start": v(-825, -9.5) * mm, "end": v(-20, -9.5) * mm});
            skCircle(sketch, "E87", {"center": v(-100, 15) * mm, "radius": 6.5 * mm});
            skCircle(sketch, "E88", {"center": v(-800, 15) * mm, "radius": 6.5 * mm});
            skCircle(sketch, "E89", {"center": v(-800, 765) * mm, "radius": 6.5 * mm});
            skCircle(sketch, "E90", {"center": v(-100, 765) * mm, "radius": 6.5 * mm});
            skSolve(sketch);
        }
        {
            var Q0;
            {var subQ2=sQuery(id+"F69.wireOp",EDGE,"E85.top");Q0=makeQuery(id+"F69.imprint","IMPRINT",FACE,{"disambiguationData":[TD([[makeQuery(id+"F69.imprint","IMPRINT",EDGE,{"derivedFrom":subQ2}),-1.0]])]});}
            var Q1;
            {var subQ2=sQuery(id+"F69.wireOp",EDGE,"E86");Q1=makeQuery(id+"F69.imprint","IMPRINT",FACE,{"disambiguationData":[TD([[makeQuery(id+"F69.imprint","IMPRINT",EDGE,{"derivedFrom":subQ2}),1.0]])]});}
            extrude(context, id + "F70", {"entities" : qUnion([Q0, Q1]), "depth" : 2.5 * mm});
        }
        {
            var Q0;
            Q0=makeQuery(id+"F70.opExtrude","CAP_FACE",FACE,{"disambiguationData":[OSD([sQuery(id+"F69.wireOp",EDGE,"E85.top"),sQuery(id+"F69.wireOp",EDGE,"E85.left"),sQuery(id+"F69.wireOp",EDGE,"E85.right"),sQuery(id+"F69.wireOp",EDGE,"E86"),sQuery(id+"F69.wireOp",EDGE,"E87"),sQuery(id+"F69.wireOp",EDGE,"E88"),sQuery(id+"F69.wireOp",EDGE,"E89"),sQuery(id+"F69.wireOp",EDGE,"E90")])],"isStart":false});
            var sketch = newSketch(context, id + "F71", { "sketchPlane" : qUnion([Q0])});
            skLineSegment(sketch, "E91.bottom", {"start": v(-825, 788.5) * mm, "end": v(-20, 788.5) * mm});
            skLineSegment(sketch, "E91.top", {"start": v(-825, 786) * mm, "end": v(-20, 786) * mm});
            skLineSegment(sketch, "E91.left", {"start": v(-825, 788.5) * mm, "end": v(-825, 786) * mm});
            skLineSegment(sketch, "E91.right", {"start": v(-20, 788.5) * mm, "end": v(-20, 786) * mm});
            skLineSegment(sketch, "E92.bottom", {"start": v(-20, -9.5) * mm, "end": v(-825, -9.5) * mm});
            skLineSegment(sketch, "E92.top", {"start": v(-20, -7) * mm, "end": v(-825, -7) * mm});
            skLineSegment(sketch, "E92.left", {"start": v(-20, -9.5) * mm, "end": v(-20, -7) * mm});
            skLineSegment(sketch, "E92.right", {"start": v(-825, -9.5) * mm, "end": v(-825, -7) * mm});
            skSolve(sketch);
        }
        {
            var Q0;
            Q0=makeQuery(id+"F71.imprint","IMPRINT",FACE,{"disambiguationData":[TD([[makeQuery(id+"F71.imprint","IMPRINT",EDGE,{"derivedFrom":sQuery(id+"F71.wireOp",EDGE,"E92.bottom")}),1.0]])]});
            var Q1;
            Q1=makeQuery(id+"F71.imprint","IMPRINT",FACE,{"disambiguationData":[TD([[makeQuery(id+"F71.imprint","IMPRINT",EDGE,{"derivedFrom":sQuery(id+"F71.wireOp",EDGE,"E91.bottom")}),-1.0]])]});
            extrude(context, id + "F72", {"entities" : qUnion([Q0, Q1]), "operationType" : NewBodyOperationType.ADD, "depth" : 42 * mm});
        }
        {
            var Q0;
            Q0=makeQuery(id+"F11.opExtrude","CAP_FACE",FACE,{"disambiguationData":[OSD([sQuery(id+"F10.wireOp",EDGE,"E20.bottom"),sQuery(id+"F10.wireOp",EDGE,"E20.top"),sQuery(id+"F10.wireOp",EDGE,"E20.left"),sQuery(id+"F10.wireOp",EDGE,"E20.right")])],"isStart":true});
            var sketch = newSketch(context, id + "F73", { "sketchPlane" : qUnion([Q0])});
            skCircle(sketch, "E93", {"center": v(-750, 41) * mm, "radius": 6.5 * mm});
            skCircle(sketch, "E94", {"center": v(-700, 41) * mm, "radius": 6.5 * mm});
            skCircle(sketch, "E95", {"center": v(-150, 41) * mm, "radius": 6.5 * mm});
            skSolve(sketch);
        }
        {
            var Q0;
            Q0 = qSketchRegion(id + "F73", true);
            extrude(context, id + "F74", {"entities" : qUnion([Q0]), "operationType" : NewBodyOperationType.REMOVE, "endBound" : BoundingType.THROUGH_ALL, "oppositeDirection" : true, "depth" : 25 * mm, "hasSecondDirection" : true, "secondDirectionBound" : SecondDirectionBoundingType.THROUGH_ALL, "secondDirectionOppositeDirection" : false, "secondDirectionDepth" : 25 * mm});
        }
        {
            var Q0;
            Q0=makeQuery(id+"F72.boolean.opBoolean","MERGE",FACE,{"derivedFrom":[makeQuery(id+"F70.opExtrude","SWEPT_FACE",FACE,{"disambiguationData":[OSD([sQuery(id+"F69.wireOp",EDGE,"E85.left")])]}),makeQuery(id+"F72.opExtrude","SWEPT_FACE",FACE,{"disambiguationData":[OSD([sQuery(id+"F71.wireOp",EDGE,"E91.left")])]}),makeQuery(id+"F72.opExtrude","SWEPT_FACE",FACE,{"disambiguationData":[OSD([sQuery(id+"F71.wireOp",EDGE,"E92.right")])]})]});
            extrude(context, id + "F75", {"entities" : qUnion([Q0]), "depth" : 870 * mm});
        }
        {
            var Q0;
            Q0=makeQuery(id+"F72.boolean.opBoolean","MERGE",FACE,{"derivedFrom":[makeQuery(id+"F70.opExtrude","SWEPT_FACE",FACE,{"disambiguationData":[OSD([sQuery(id+"F69.wireOp",EDGE,"E86")])]}),makeQuery(id+"F72.opExtrude","SWEPT_FACE",FACE,{"disambiguationData":[OSD([sQuery(id+"F71.wireOp",EDGE,"E92.bottom")])]})]});
            var sketch = newSketch(context, id + "F76", { "sketchPlane" : qUnion([Q0])});
            skCircle(sketch, "E96", {"center": v(-750, 41) * mm, "radius": 3.18 * mm});
            skCircle(sketch, "E97", {"center": v(-950, 41) * mm, "radius": 6.5 * mm});
            skCircle(sketch, "E98", {"center": v(-900, 41) * mm, "radius": 6.5 * mm});
            skCircle(sketch, "E99", {"center": v(-1570, 41) * mm, "radius": 6.5 * mm});
            skCircle(sketch, "E100", {"center": v(-1620, 41) * mm, "radius": 6.5 * mm});
            skSolve(sketch);
        }
        {
            var Q0;
            Q0 = qSketchRegion(id + "F76", true);
            extrude(context, id + "F77", {"entities" : qUnion([Q0]), "operationType" : NewBodyOperationType.REMOVE, "endBound" : BoundingType.THROUGH_ALL, "oppositeDirection" : true, "depth" : 25 * mm});
        }
        {
            var Q0;
            Q0=makeQuery(id+"F70.opExtrude","CAP_FACE",FACE,{"disambiguationData":[OSD([sQuery(id+"F69.wireOp",EDGE,"E85.top"),sQuery(id+"F69.wireOp",EDGE,"E85.left"),sQuery(id+"F69.wireOp",EDGE,"E85.right"),sQuery(id+"F69.wireOp",EDGE,"E86"),sQuery(id+"F69.wireOp",EDGE,"E87"),sQuery(id+"F69.wireOp",EDGE,"E88"),sQuery(id+"F69.wireOp",EDGE,"E89"),sQuery(id+"F69.wireOp",EDGE,"E90")])],"isStart":false});
            var sketch = newSketch(context, id + "F78", { "sketchPlane" : qUnion([Q0])});
            skCircle(sketch, "E101", {"center": v(-800, 765) * mm, "radius": 4.65 * mm});
            skCircle(sketch, "E102", {"center": v(-850, 765) * mm, "radius": 6.5 * mm});
            skCircle(sketch, "E103", {"center": v(-1670, 765) * mm, "radius": 6.5 * mm});
            skCircle(sketch, "E104", {"center": v(-800, 15) * mm, "radius": 3.65 * mm});
            skCircle(sketch, "E105", {"center": v(-850, 15) * mm, "radius": 6.5 * mm});
            skCircle(sketch, "E106", {"center": v(-1670, 15) * mm, "radius": 6.5 * mm});
            skSolve(sketch);
        }
        {
            var Q0;
            Q0 = qSketchRegion(id + "F78", true);
            extrude(context, id + "F79", {"entities" : qUnion([Q0]), "operationType" : NewBodyOperationType.REMOVE, "oppositeDirection" : true, "depth" : 25 * mm});
        }
        {
            var Q0;
            Q0=makeQuery(id+"F75.opExtrude","SWEPT_BODY",BODY,{"disambiguationData":[OSD([sQuery(id+"F69.wireOp",EDGE,"E85.left"),sQuery(id+"F71.wireOp",EDGE,"E91.left"),sQuery(id+"F71.wireOp",EDGE,"E92.right")])]});
            transform(context, id + "F80", {"entities" : qUnion([Q0]), "transformType" : TransformType.TRANSLATION_3D, "dx" : -870 * mm, "dy" : 0 * mm, "dz" : 0 * mm, "makeCopy" : true});
        }
        {
            var Q0;
            Q0=makeQuery(id+"F80.opPattern","COPY",FACE,{"derivedFrom":makeQuery(id+"F75.opExtrude","SWEPT_FACE",FACE,{"disambiguationData":[OSD([sQuery(id+"F69.wireOp",EDGE,"E85.left"),sQuery(id+"F69.wireOp",EDGE,"E86"),sQuery(id+"F71.wireOp",EDGE,"E92.bottom"),sQuery(id+"F71.wireOp",EDGE,"E92.right")])]}),"instanceName":"1"});
            var sketch = newSketch(context, id + "F81", { "sketchPlane" : qUnion([Q0])});
            skCircle(sketch, "E107", {"center": v(-2490, 41) * mm, "radius": 6.5 * mm});
            skCircle(sketch, "E108", {"center": v(-2440, 41) * mm, "radius": 6.5 * mm});
            skLineSegment(sketch, "E109", {"start": v(-2515.5, 64.5) * mm, "end": v(-2565, 64.5) * mm});
            skLineSegment(sketch, "E110", {"start": v(-2565, 64.5) * mm, "end": v(-2565, 20) * mm});
            skLineSegment(sketch, "E111", {"start": v(-2515.5, 64.5) * mm, "end": v(-2560, 20) * mm});
            skLineSegment(sketch, "E112", {"start": v(-2560, 20) * mm, "end": v(-2565, 20) * mm});
            skSolve(sketch);
        }
        {
            var Q0;
            Q0=makeQuery(id+"F81.imprint","IMPRINT",FACE,{"disambiguationData":[TD([[makeQuery(id+"F81.imprint","IMPRINT",EDGE,{"derivedFrom":sQuery(id+"F81.wireOp",EDGE,"E109")}),-1.0]])]});
            extrude(context, id + "F82", {"entities" : qUnion([Q0]), "operationType" : NewBodyOperationType.REMOVE, "endBound" : BoundingType.THROUGH_ALL, "oppositeDirection" : true, "depth" : 25 * mm});
        }
        {
            var Q0;
            Q0=makeQuery(id+"F81.imprint","IMPRINT",FACE,{"disambiguationData":[TD([[makeQuery(id+"F81.imprint","IMPRINT",EDGE,{"derivedFrom":sQuery(id+"F81.wireOp",EDGE,"E107")}),1.0]])]});
            var Q1;
            Q1=makeQuery(id+"F81.imprint","IMPRINT",FACE,{"disambiguationData":[TD([[makeQuery(id+"F81.imprint","IMPRINT",EDGE,{"derivedFrom":sQuery(id+"F81.wireOp",EDGE,"E108")}),1.0]])]});
            extrude(context, id + "F83", {"entities" : qUnion([Q0, Q1]), "operationType" : NewBodyOperationType.ADD, "oppositeDirection" : true, "depth" : 2.5 * mm});
        }
        {
            var Q0;
            Q0=makeQuery(id+"F80.opPattern","COPY",FACE,{"derivedFrom":makeQuery(id+"F75.opExtrude","SWEPT_FACE",FACE,{"disambiguationData":[OSD([sQuery(id+"F69.wireOp",EDGE,"E85.left"),sQuery(id+"F71.wireOp",EDGE,"E91.top"),sQuery(id+"F71.wireOp",EDGE,"E91.left")])]}),"instanceName":"1"});
            var sketch = newSketch(context, id + "F84", { "sketchPlane" : qUnion([Q0])});
            skCircle(sketch, "E113", {"center": v(-2490, 41) * mm, "radius": 6.5 * mm});
            skCircle(sketch, "E114", {"center": v(-2440, 41) * mm, "radius": 6.5 * mm});
            skSolve(sketch);
        }
        {
            var Q0;
            Q0 = qSketchRegion(id + "F84", true);
            extrude(context, id + "F85", {"entities" : qUnion([Q0]), "operationType" : NewBodyOperationType.ADD, "oppositeDirection" : true, "depth" : 2.5 * mm});
        }
    });
